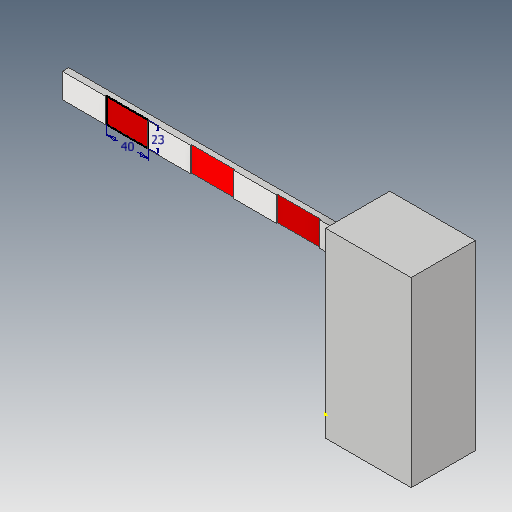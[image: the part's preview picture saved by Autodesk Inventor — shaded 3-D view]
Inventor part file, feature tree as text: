
AUTODESK INVENTOR PART (.ipt)
format: ipt  version: 2018 (Build 220112000, 112)  size: 172,032 bytes
history: native  units: in
note: dims shown in document units (in); Inventor stores cm internally (conversion verified against a paired STEP export)
features: sketch x12, extrude x7
ambient origin geometry x8: Origin, YZ Plane, XZ Plane, XY Plane, X Axis, Y Axis, Z Axis, Center Point
bodies: Solid1 (feature_tree)
feature tree (19):
  sketch  "Sketch1"  dims[d0=11.811in d1=0.9055in]
  extrude  "Extrusion1"  Depth=0.9055in
  sketch  "Sketch3"  dims[d4=1.1811in d5=0.7874in]
  sketch  "Sketch4"  dims[d6=0.1969in d7=0.0in d8=3.1496in]
  extrude  "Extrusion2"  Depth=5.9055in
  extrude  "Extrusion3"  Depth=0.7874in
  sketch  "Sketch7"  dims[d14=0.0394in d15=0.0in d16=1.5748in]
  extrude  "Extrusion4"  Depth=3.1496in
  extrude  "Extrusion5"  Depth=2.3622in TaperAngle=0.0deg
  extrude  "Extrusion6"  Depth=0.9055in
  sketch  "Sketch11"  dims[d20=1.5748in]
  extrude  "Extrusion7"  Depth=1.5748in
  sketch  "Sketch2"  dims[d2=3.1496in d3=5.9055in]
  sketch  "Sketch5"  dims[d9=5.9055in d10=2.3622in d11=0.0in]
  sketch  "Sketch6"  dims[d12=1.5748in d13=0.9055in]
  sketch  "Sketch8"  dims[d17=0.9055in]
  sketch  "Sketch9"  dims[d18=1.5748in]
  sketch  "Sketch10"  dims[d19=0.9055in]
  sketch  "Sketch12"  dims[d21=0.9055in d22=0.0394in d23=0.0in d24=1.5748in d25=0.9055in d26=1.5748in d27=0.9055in d28=0.0394in d29=0.0in d30=1.5748in d31=0.9055in d32=1.1811in d33=0.9055in d34=0.0394in d35=0.0in d36=0.7874in d37=2.3622in d38=0.0in]
